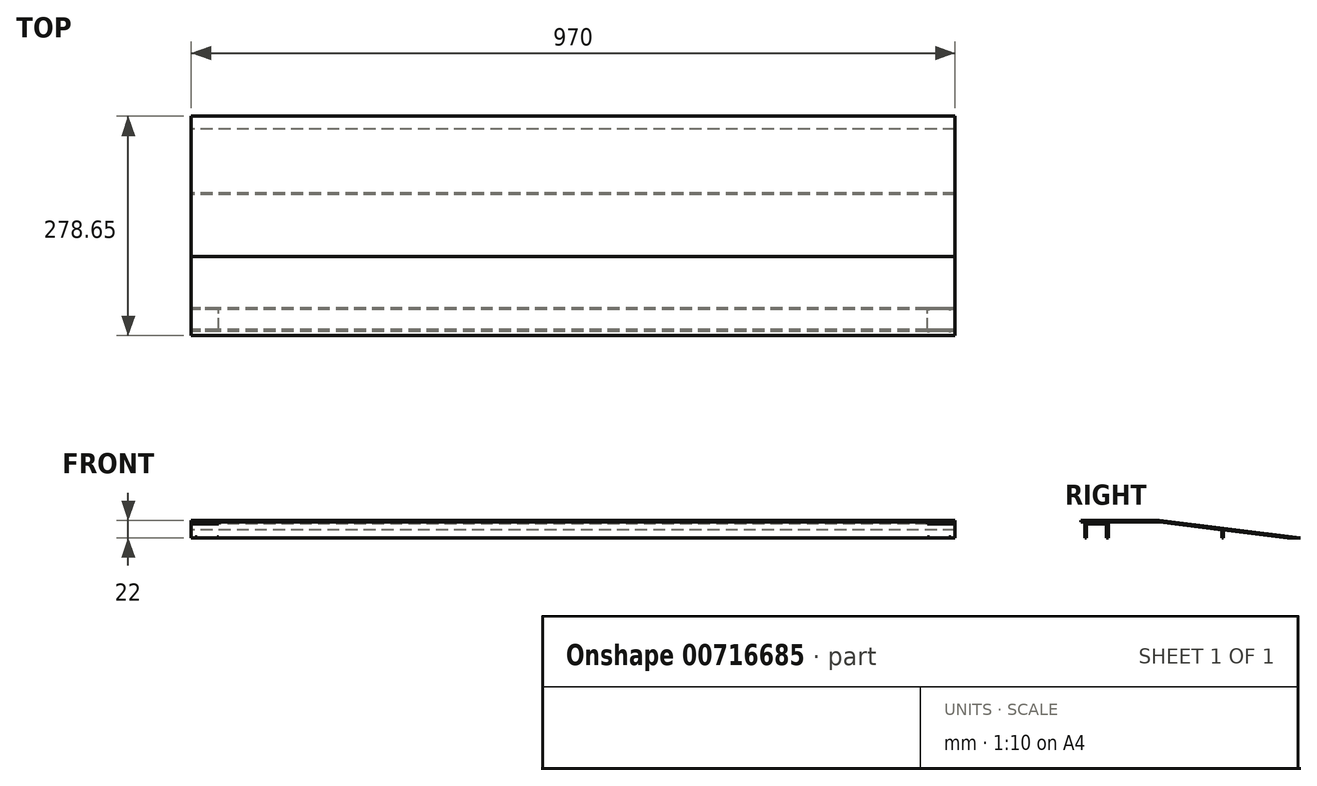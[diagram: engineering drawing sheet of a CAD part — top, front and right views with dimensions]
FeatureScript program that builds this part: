
annotation { "Feature Type Name" : "Feature", "Feature Type Description" : "" }
export const myFeature = defineFeature(function(context is Context, id is Id, definition is map)
    precondition{}
    {
        {
            var Q0;
            Q0=qCreatedBy(makeId("Right.planeOp"),FACE);
            var sketch = newSketch(context, id + "F0", { "sketchPlane" : qUnion([Q0])});
            skLineSegment(sketch, "E0.bottom", {"start": v(0, 0) * mm, "end": v(2.3, 0) * mm});
            skLineSegment(sketch, "E0.top", {"start": v(0, 20) * mm, "end": v(30, 20) * mm});
            skLineSegment(sketch, "E0.left", {"start": v(0, 0) * mm, "end": v(0, 20) * mm});
            skLineSegment(sketch, "E0.right", {"start": v(30, 0) * mm, "end": v(30, 20) * mm});
            skLineSegment(sketch, "E1.0", {"start": v(27.7, 0) * mm, "end": v(27.7, 17.7) * mm});
            skLineSegment(sketch, "E2.0", {"start": v(2.3, 17.7) * mm, "end": v(27.7, 17.7) * mm});
            skLineSegment(sketch, "E3.0", {"start": v(2.3, 0) * mm, "end": v(2.3, 17.7) * mm});
            skLineSegment(sketch, "E4.trimOffspring", {"start": v(27.7, 0) * mm, "end": v(30, 0) * mm});
            skSolve(sketch);
        }
        {
            var Q0;
            Q0=qSketchRegion(id+"F0",true);
            extrude(context, id + "F1", {"entities" : qUnion([Q0]), "depth" : 970 * mm, "offsetDistance" : 25 * mm});
        }
        {
            var Q0;
            Q0=makeQuery(id+"F1.opExtrude","SWEPT_FACE",FACE,{"disambiguationData":[OSD([sQuery(id+"F0.wireOp",EDGE,"E0.top")])]});
            var sketch = newSketch(context, id + "F2", { "sketchPlane" : qUnion([Q0])});
            skLineSegment(sketch, "E5.bottom", {"start": v(0, 0) * mm, "end": v(35, 0) * mm});
            skLineSegment(sketch, "E5.top", {"start": v(0, 30) * mm, "end": v(35, 30) * mm});
            skLineSegment(sketch, "E5.left", {"start": v(0, 0) * mm, "end": v(0, 30) * mm});
            skLineSegment(sketch, "E5.right", {"start": v(35, 0) * mm, "end": v(35, 30) * mm});
            skLineSegment(sketch, "E6.bottom", {"start": v(970, 0) * mm, "end": v(935, 0) * mm});
            skLineSegment(sketch, "E6.top", {"start": v(970, 30) * mm, "end": v(935, 30) * mm});
            skLineSegment(sketch, "E6.left", {"start": v(970, 0) * mm, "end": v(970, 30) * mm});
            skLineSegment(sketch, "E6.right", {"start": v(935, 0) * mm, "end": v(935, 30) * mm});
            skSolve(sketch);
        }
        {
            var Q0;
            Q0=qSketchRegion(id+"F2",true);
            extrude(context, id + "F3", {"entities" : qUnion([Q0]), "operationType" : NewBodyOperationType.REMOVE, "oppositeDirection" : true, "depth" : 2.3 * mm, "offsetDistance" : 25 * mm});
        }
        {
            var Q0;
            Q0=makeQuery(id+"F1.opExtrude","SWEPT_FACE",FACE,{"disambiguationData":[OSD([sQuery(id+"F0.wireOp",EDGE,"E0.left")])]});
            var sketch = newSketch(context, id + "F4", { "sketchPlane" : qUnion([Q0])});
            skLineSegment(sketch, "E7.bottom", {"start": v(35, 0) * mm, "end": v(32.6, 0) * mm});
            skLineSegment(sketch, "E7.top", {"start": v(35, 1) * mm, "end": v(32.6, 1) * mm});
            skLineSegment(sketch, "E7.left", {"start": v(35, 0) * mm, "end": v(35, 1) * mm});
            skLineSegment(sketch, "E7.right", {"start": v(32.6, 0) * mm, "end": v(32.6, 1) * mm});
            skLineSegment(sketch, "E8.bottom", {"start": v(7.4, 0) * mm, "end": v(5, 0) * mm});
            skLineSegment(sketch, "E8.top", {"start": v(7.4, 1) * mm, "end": v(5, 1) * mm});
            skLineSegment(sketch, "E8.left", {"start": v(7.4, 0) * mm, "end": v(7.4, 1) * mm});
            skLineSegment(sketch, "E8.right", {"start": v(5, 0) * mm, "end": v(5, 1) * mm});
            skLineSegment(sketch, "E9", {"start": v(485, 128) * mm, "end": v(485, 0) * mm, "construction": true});
            skLineSegment(sketch, "E10.MirrorCS", {"start": v(937.4, 0) * mm, "end": v(937.4, 1) * mm});
            skLineSegment(sketch, "E11.MirrorCS", {"start": v(935, 1) * mm, "end": v(937.4, 1) * mm});
            skLineSegment(sketch, "E12.MirrorCS", {"start": v(935, 0) * mm, "end": v(935, 1) * mm});
            skLineSegment(sketch, "E13.MirrorCS", {"start": v(965, 0) * mm, "end": v(965, 1) * mm});
            skLineSegment(sketch, "E14.MirrorCS", {"start": v(962.6, 1) * mm, "end": v(965, 1) * mm});
            skLineSegment(sketch, "E15.MirrorCS", {"start": v(962.6, 0) * mm, "end": v(962.6, 1) * mm});
            skLineSegment(sketch, "E16.MirrorCS", {"start": v(962.6, 0) * mm, "end": v(965, 0) * mm});
            skLineSegment(sketch, "E17.MirrorCS", {"start": v(935, 0) * mm, "end": v(937.4, 0) * mm});
            skSolve(sketch);
        }
        {
            var Q0;
            Q0=qSketchRegion(id+"F4",true);
            extrude(context, id + "F5", {"entities" : qUnion([Q0]), "operationType" : NewBodyOperationType.REMOVE, "endBound" : BoundingType.THROUGH_ALL, "oppositeDirection" : true, "depth" : 25 * mm, "offsetDistance" : 25 * mm});
        }
        {
            var Q0;
            Q0=qCreatedBy(makeId("Right.planeOp"),FACE);
            var sketch = newSketch(context, id + "F6", { "sketchPlane" : qUnion([Q0])});
            skLineSegment(sketch, "E18.bottom", {"start": v(95, 20) * mm, "end": v(-5, 20) * mm});
            skLineSegment(sketch, "E18.top", {"start": v(95, 22) * mm, "end": v(-5, 22) * mm});
            skLineSegment(sketch, "E19", {"start": v(95, 22) * mm, "end": v(273.65, 0) * mm});
            skLineSegment(sketch, "E20", {"start": v(95, 20) * mm, "end": v(257.4, 0) * mm});
            skLineSegment(sketch, "E21", {"start": v(257.4, 0) * mm, "end": v(273.65, 0) * mm});
            skLineSegment(sketch, "E22", {"start": v(0, 0) * mm, "end": v(226.36, 0) * mm, "construction": true});
            skLineSegment(sketch, "E23", {"start": v(176.2, 10) * mm, "end": v(176.2, 0) * mm});
            skLineSegment(sketch, "E24", {"start": v(174.2, 10.25) * mm, "end": v(174.2, 0) * mm});
            skLineSegment(sketch, "E25", {"start": v(174.2, 0) * mm, "end": v(176.2, 0) * mm});
            skLineSegment(sketch, "E26", {"start": v(15, 37) * mm, "end": v(15, -23.89) * mm, "construction": true});
            skLineSegment(sketch, "E27", {"start": v(-5, 22) * mm, "end": v(-5, 20) * mm});
            skLineSegment(sketch, "E28", {"start": v(175.2, 0) * mm, "end": v(175.2, 15.02) * mm, "construction": true});
            skSolve(sketch);
        }
        {
            var Q0;
            Q0 = qSketchRegion(id + "F6", true);
            extrude(context, id + "F7", {"entities" : qUnion([Q0]), "depth" : 970 * mm, "offsetDistance" : 25 * mm});
        }
    });
